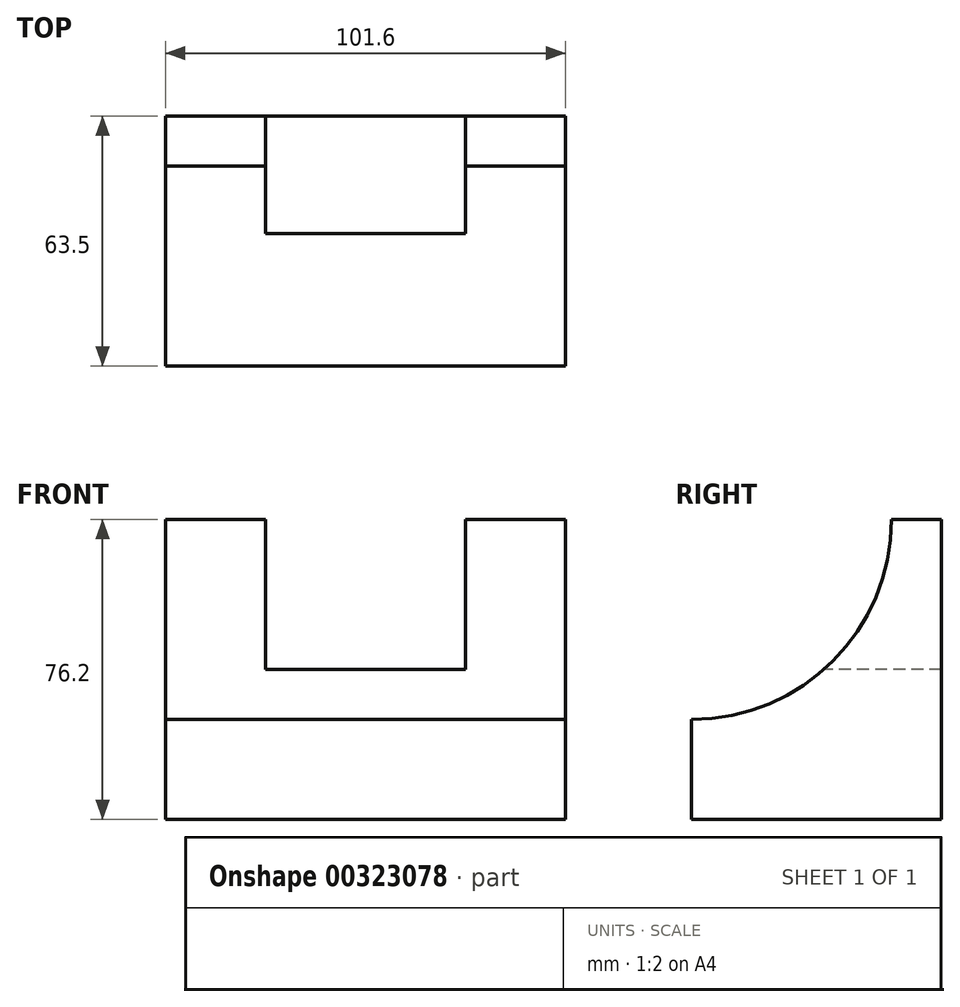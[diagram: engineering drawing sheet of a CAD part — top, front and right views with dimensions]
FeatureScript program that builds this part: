
annotation { "Feature Type Name" : "Feature", "Feature Type Description" : "" }
export const myFeature = defineFeature(function(context is Context, id is Id, definition is map)
    precondition{}
    {
        {
            var Q0;
            Q0=qCreatedBy(makeId("Front.planeOp"),FACE);
            var sketch = newSketch(context, id + "F0", { "sketchPlane" : qUnion([Q0])});
            skLineSegment(sketch, "E0.bottom", {"start": v(-57.94, 38.52) * mm, "end": v(43.66, 38.52) * mm});
            skLineSegment(sketch, "E0.top", {"start": v(-57.94, -37.68) * mm, "end": v(43.66, -37.68) * mm});
            skLineSegment(sketch, "E0.left", {"start": v(-57.94, 38.52) * mm, "end": v(-57.94, -37.68) * mm});
            skLineSegment(sketch, "E0.right", {"start": v(43.66, 38.52) * mm, "end": v(43.66, -37.68) * mm});
            skSolve(sketch);
        }
        {
            var Q0;
            Q0=makeQuery(id+"F0.imprint","IMPRINT",FACE,{"disambiguationData":[TD([[makeQuery(id+"F0.imprint","IMPRINT",EDGE,{"derivedFrom":sQuery(id+"F0.wireOp",EDGE,"E0.bottom")}),-1.0]])]});
            extrude(context, id + "F1", {"entities" : qUnion([Q0]), "depth" : 63.5 * mm});
        }
        {
            var Q0;
            Q0=makeQuery(id+"F1.opExtrude","SWEPT_FACE",FACE,{"disambiguationData":[OSD([sQuery(id+"F0.wireOp",EDGE,"E0.right")])]});
            var sketch = newSketch(context, id + "F2", { "sketchPlane" : qUnion([Q0])});
            skArc(sketch, "E1", {"start": v(-63.5, -12.28) * mm, "mid": v(-27.58, 2.6) * mm, "end": v(-12.7, 38.52) * mm});
            skLineSegment(sketch, "E2", {"start": v(-63.5, -12.28) * mm, "end": v(-63.5, 38.52) * mm});
            skLineSegment(sketch, "E3", {"start": v(-12.7, 38.52) * mm, "end": v(-63.5, 38.52) * mm});
            skPoint(sketch, "E3.startSnap0", {"position": v(-31.75, 38.52) * mm});
            skSolve(sketch);
        }
        {
            var Q0;
            Q0=makeQuery(id+"F2.imprint","IMPRINT",FACE,{"disambiguationData":[TD([[makeQuery(id+"F2.imprint","IMPRINT",EDGE,{"derivedFrom":sQuery(id+"F2.wireOp",EDGE,"E1")}),1.0]])]});
            extrude(context, id + "F3", {"entities" : qUnion([Q0]), "operationType" : NewBodyOperationType.REMOVE, "endBound" : BoundingType.THROUGH_ALL, "oppositeDirection" : true, "depth" : 25.4 * mm});
        }
        {
            var Q0;
            Q0=makeQuery(id+"F1.opExtrude","SWEPT_FACE",FACE,{"disambiguationData":[OSD([sQuery(id+"F0.wireOp",EDGE,"E0.bottom")])]});
            var sketch = newSketch(context, id + "F4", { "sketchPlane" : qUnion([Q0])});
            skLineSegment(sketch, "E4.bottom", {"start": v(-32.54, 0) * mm, "end": v(18.26, 0) * mm});
            skLineSegment(sketch, "E4.top", {"start": v(-32.54, -12.7) * mm, "end": v(18.26, -12.7) * mm});
            skLineSegment(sketch, "E4.left", {"start": v(-32.54, 0) * mm, "end": v(-32.54, -12.7) * mm});
            skLineSegment(sketch, "E4.right", {"start": v(18.26, 0) * mm, "end": v(18.26, -12.7) * mm});
            skSolve(sketch);
        }
        {
            var Q0;
            Q0=makeQuery(id+"F4.imprint","IMPRINT",FACE,{"disambiguationData":[TD([[makeQuery(id+"F4.imprint","IMPRINT",EDGE,{"derivedFrom":sQuery(id+"F4.wireOp",EDGE,"E4.bottom")}),-1.0]])]});
            extrude(context, id + "F5", {"entities" : qUnion([Q0]), "operationType" : NewBodyOperationType.REMOVE, "oppositeDirection" : true, "depth" : 38.1 * mm});
        }
        {
            var Q0;
            Q0=makeQuery(id+"F5.boolean.opBoolean","COPY",FACE,{"derivedFrom":makeQuery(id+"F5.opExtrude","SWEPT_FACE",FACE,{"disambiguationData":[OSD([sQuery(id+"F4.wireOp",EDGE,"E4.top")])]})});
            extrude(context, id + "F6", {"entities" : qUnion([Q0]), "operationType" : NewBodyOperationType.REMOVE, "endBound" : BoundingType.THROUGH_ALL, "oppositeDirection" : true, "depth" : 25.4 * mm});
        }
    });
